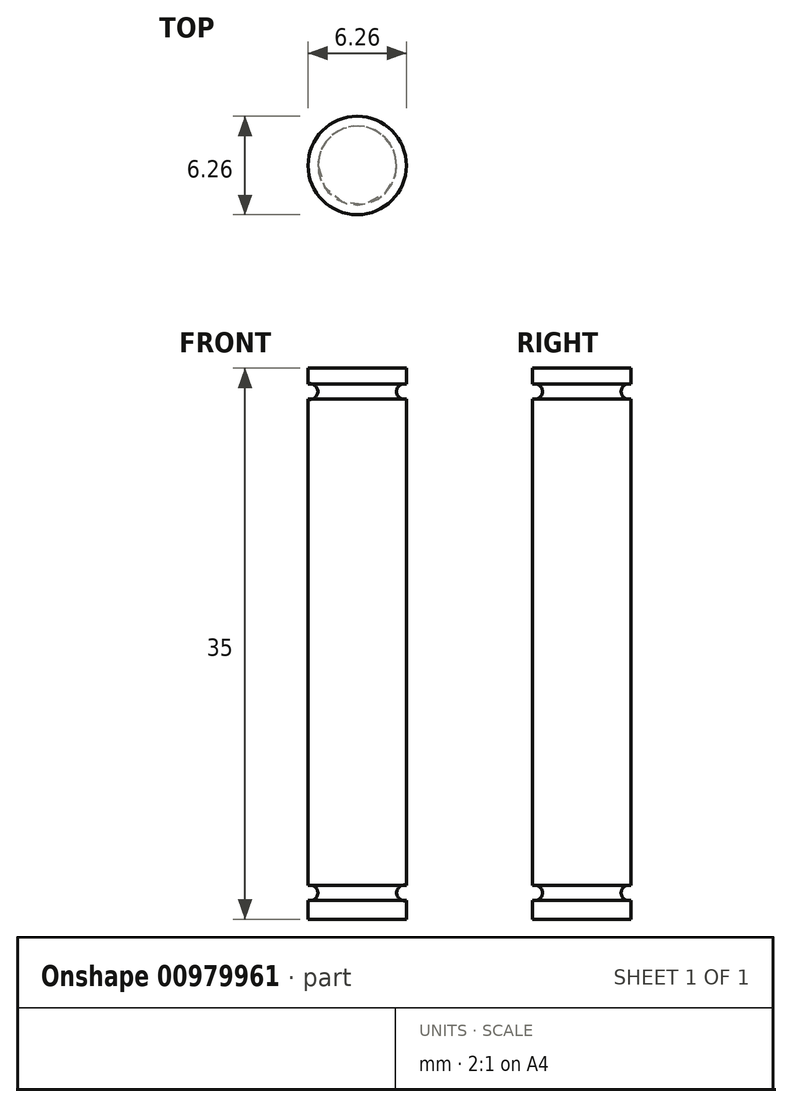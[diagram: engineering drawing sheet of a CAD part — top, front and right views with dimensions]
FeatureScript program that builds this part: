
annotation { "Feature Type Name" : "Feature", "Feature Type Description" : "" }
export const myFeature = defineFeature(function(context is Context, id is Id, definition is map)
    precondition{}
    {
        {
            var Q0;
            Q0=qCreatedBy(makeId("Top.planeOp"),FACE);
            var sketch = newSketch(context, id + "F0", { "sketchPlane" : qUnion([Q0])});
            skCircle(sketch, "E0", {"center": v(0, 0) * mm, "radius": 3.13 * mm});
            skSolve(sketch);
        }
        {
            var Q0;
            Q0 = qSketchRegion(id + "F0", true);
            extrude(context, id + "F1", {"entities" : qUnion([Q0]), "depth" : 35 * mm, "offsetDistance" : 25.4 * mm});
        }
        {
            var Q0;
            Q0=qCreatedBy(makeId("Front.planeOp"),FACE);
            var sketch = newSketch(context, id + "F2", { "sketchPlane" : qUnion([Q0])});
            skLineSegment(sketch, "E1", {"start": v(0, -5.89) * mm, "end": v(0, 5.95) * mm});
            skCircle(sketch, "E2", {"center": v(-3, 1.68) * mm, "radius": 0.5 * mm});
            skSolve(sketch);
        }
        {
            var Q0;
            Q0=makeQuery(id+"F2.imprint","IMPRINT",FACE,{"disambiguationData":[TD([[makeQuery(id+"F2.imprint","IMPRINT",EDGE,{"derivedFrom":sQuery(id+"F2.wireOp",EDGE,"E2")}),1.0]])]});
            var Q1;
            Q1=sQuery(id+"F2.wireOp",EDGE,"E2");
            var Q2;
            Q2=sQuery(id+"F2.wireOp",EDGE,"E1");
            revolve(context, id + "F3", {"operationType" : NewBodyOperationType.REMOVE, "surfaceOperationType" : NewSurfaceOperationType.NEW, "entities" : qUnion([Q0]), "surfaceEntities" : qUnion([Q1]), "axis" : qUnion([Q2]), "revolveType" : RevolveType.FULL, "oppositeDirection" : true});
        }
        {
            var Q0;
            Q0=qCreatedBy(makeId("Front.planeOp"),FACE);
            var sketch = newSketch(context, id + "F4", { "sketchPlane" : qUnion([Q0])});
            skLineSegment(sketch, "E3", {"start": v(0, 0) * mm, "end": v(0, 41.94) * mm});
            skCircle(sketch, "E4", {"center": v(-3, 33.52) * mm, "radius": 0.5 * mm});
            skSolve(sketch);
        }
        {
            var Q0;
            Q0=makeQuery(id+"F4.imprint","IMPRINT",FACE,{"disambiguationData":[TD([[makeQuery(id+"F4.imprint","IMPRINT",EDGE,{"derivedFrom":sQuery(id+"F4.wireOp",EDGE,"E4")}),1.0]])]});
            var Q1;
            Q1=sQuery(id+"F4.wireOp",EDGE,"E3");
            revolve(context, id + "F5", {"operationType" : NewBodyOperationType.REMOVE, "surfaceOperationType" : NewSurfaceOperationType.NEW, "entities" : qUnion([Q0]), "axis" : qUnion([Q1]), "revolveType" : RevolveType.FULL, "oppositeDirection" : true});
        }
    });
